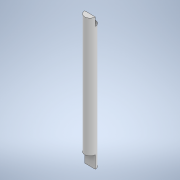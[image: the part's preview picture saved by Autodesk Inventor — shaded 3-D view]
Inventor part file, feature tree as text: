
AUTODESK INVENTOR PART (.ipt)
format: ipt  version: 2022 (Build 260153000, 153)  size: 107,520 bytes
history: native  units: mm
features: extrude x3, sketch x3
ambient origin geometry x8: Origin, YZ Plane, XZ Plane, XY Plane, X Axis, Y Axis, Z Axis, Center Point
bodies: Solid1 (feature_tree)
feature tree (6):
  extrude  "Extrusion1"  Depth=65.0mm TaperAngle=0.0deg
  extrude  "Extrusion2"  Depth=6.2mm TaperAngle=0.0deg
  extrude  "Extrusion3"  [1 undecoded]
  sketch  "Sketch1"  dims[d0=5.25mm d1=65.0mm d2=0.0mm]
  sketch  "Sketch2"  dims[d3=4.0mm d4=0.0mm d5=6.2mm d6=0.0mm]
  sketch  "Sketch3"
note: 1 required parameter value undecoded (feature->parameter linkage not recoverable at this tier; creation-order binding heuristic only, values carry confidence <= 0.55)
